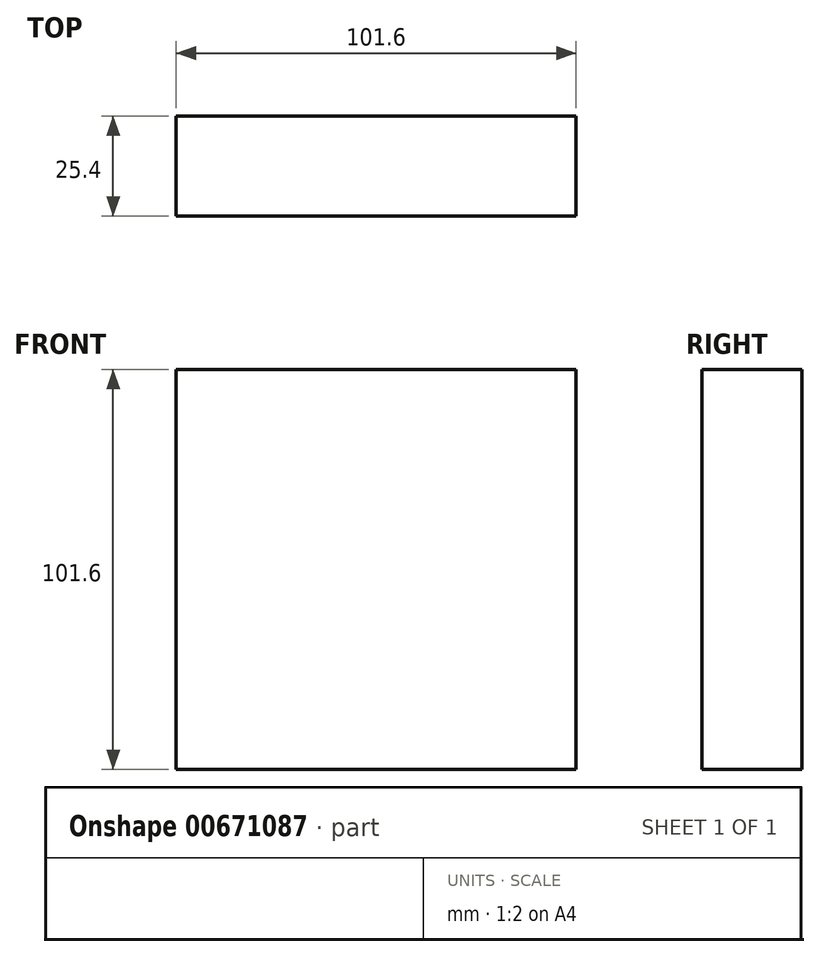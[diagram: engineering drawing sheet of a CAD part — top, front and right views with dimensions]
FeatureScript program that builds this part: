
annotation { "Feature Type Name" : "Feature", "Feature Type Description" : "" }
export const myFeature = defineFeature(function(context is Context, id is Id, definition is map)
    precondition{}
    {
        {
            var Q0;
            Q0=qCreatedBy(makeId("Front.planeOp"),FACE);
            var sketch = newSketch(context, id + "F0", { "sketchPlane" : qUnion([Q0])});
            skLineSegment(sketch, "E0.bottom", {"start": v(-50.8, 55.47) * mm, "end": v(50.8, 55.47) * mm});
            skLineSegment(sketch, "E0.top", {"start": v(-50.8, -46.13) * mm, "end": v(50.8, -46.13) * mm});
            skLineSegment(sketch, "E0.left", {"start": v(-50.8, 55.47) * mm, "end": v(-50.8, -46.13) * mm});
            skLineSegment(sketch, "E0.right", {"start": v(50.8, 55.47) * mm, "end": v(50.8, -46.13) * mm});
            skPoint(sketch, "E0.middle", {"position": v(0, 4.67) * mm});
            skSolve(sketch);
        }
        {
            var Q0;
            Q0=makeQuery(id+"F0.imprint","IMPRINT",FACE,{"disambiguationData":[TD([[makeQuery(id+"F0.imprint","IMPRINT",EDGE,{"derivedFrom":sQuery(id+"F0.wireOp",EDGE,"E0.bottom")}),-1.0]])]});
            extrude(context, id + "F1", {"entities" : qUnion([Q0]), "depth" : 25.4 * mm, "offsetDistance" : 25.4 * mm});
        }
    });
